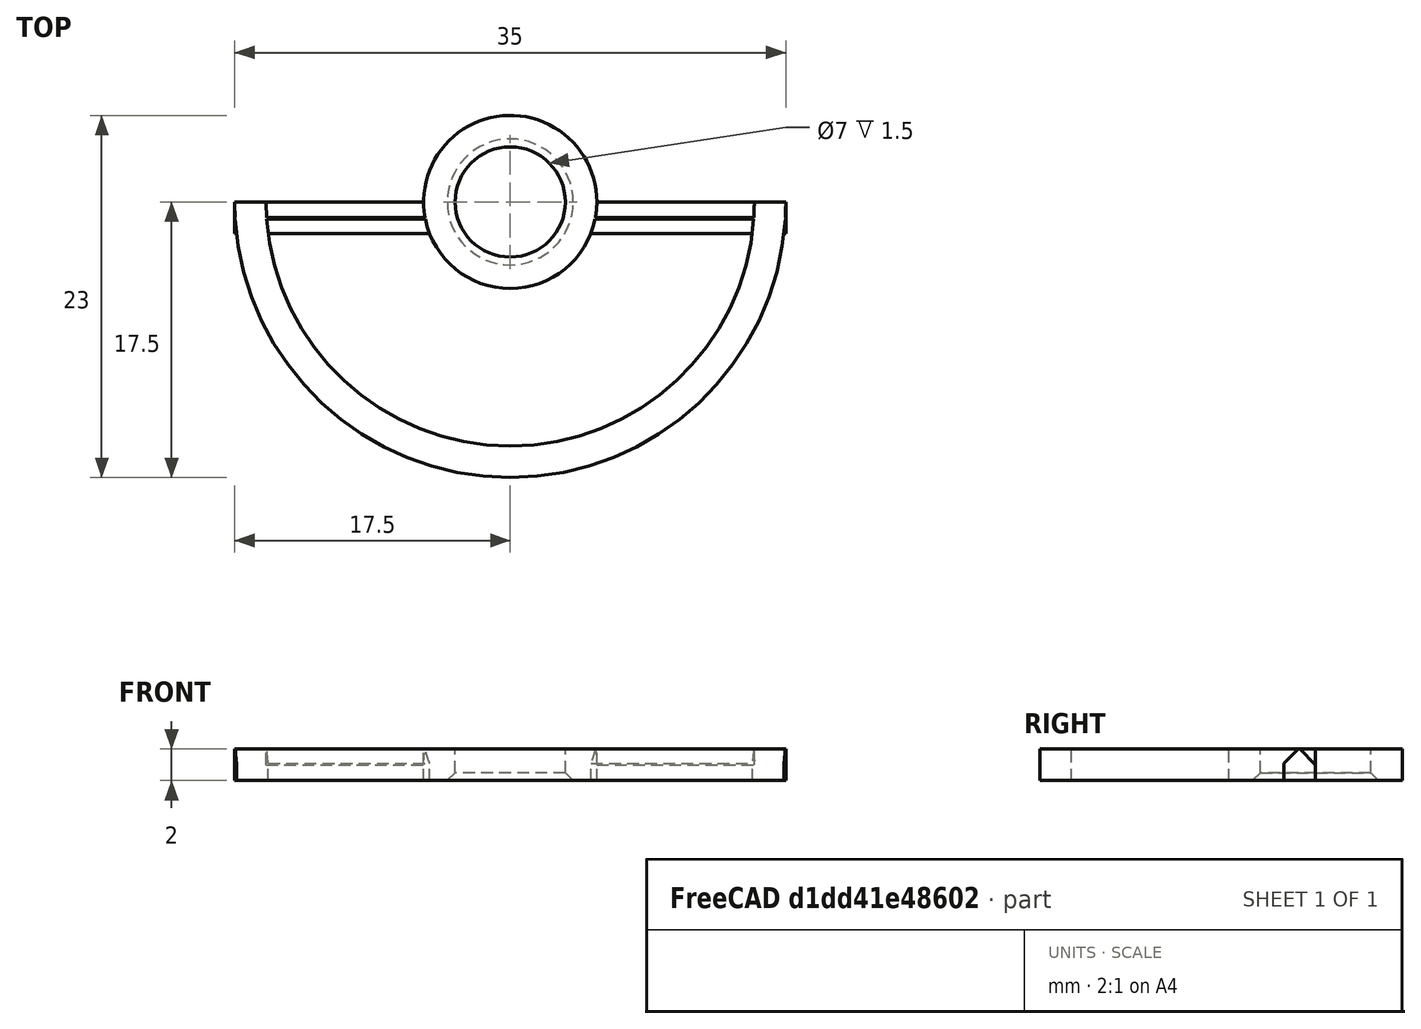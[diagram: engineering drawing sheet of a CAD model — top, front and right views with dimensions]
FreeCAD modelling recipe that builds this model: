
FCSTD DOCUMENT  (FreeCAD 0.16R6703 (Git))
Label: prop-guard
License: All rights reserved
LicenseURL: http://en.wikipedia.org/wiki/All_rights_reserved
objects: Part::Cylinder×5, Part::Chamfer×5, Part::Cut×4, Part::Box×2, Part::MultiFuse×1
note: 17 computed .brp shape members not serialized (recipe doc carries the construction recipe); baked Part::Feature solids carry a one-line shape summary decoded from their .brp

FEATURE [Part::Cylinder] Cylinder
  Angle = 360
  Height = 10
  Placement = pos=(0,0,-3) rot=(0,0,1;0rad)
  Radius = 3.5
FEATURE [Part::Cylinder] Cylinder001
  Angle = 360
  Height = 9
  Placement = pos=(0,0,-1) rot=(0,0,1;0rad)
  Radius = 15.5
FEATURE [Part::Cylinder] Cylinder002
  Angle = 360
  Height = 2
  Radius = 17.5
FEATURE [Part::Cut] Cut
  Base = -> Cylinder002
  Tool = -> Cylinder001
FEATURE [Part::Box] Box  label="Cube"
  Height = 10
  Length = 43
  Placement = pos=(-22,0,-1) rot=(0,0,1;0rad)
  Width = 27
FEATURE [Part::Cut] Cut001
  Base = -> Cut
  Tool = -> Box
FEATURE [Part::Box] Box001  label="Cube001"
  Height = 2
  Length = 35
  Placement = pos=(-17.5,-2,0) rot=(0,0,1;0rad)
  Width = 2
FEATURE [Part::Cylinder] Cylinder003
  Angle = 360
  Height = 2
  Radius = 5.5
FEATURE [Part::Cut] Cut002
  Base = -> Cylinder003
  Tool = -> Cylinder
FEATURE [Part::Cylinder] Cylinder004
  Angle = 360
  Height = 10
  Placement = pos=(0,0,-3) rot=(0,0,1;0rad)
  Radius = 5
FEATURE [Part::Cut] Cut003
  Base = -> Box001
  Tool = -> Cylinder004
FEATURE [Part::Chamfer] Chamfer
  Base = -> Cut003
  Edges = 1 edges r=1: [Edge22]
FEATURE [Part::Chamfer] Chamfer001
  Base = -> Chamfer
  Edges = 1 edges r=0.9: [Edge7]
FEATURE [Part::Chamfer] Chamfer002
  Base = -> Chamfer001
  Edges = 1 edges r=1: [Edge26]
FEATURE [Part::Chamfer] Chamfer003
  Base = -> Chamfer002
  Edges = 1 edges r=0.9: [Edge8]
FEATURE [Part::MultiFuse] Fusion  label="prop-guard-a"
  Shapes = -> [Chamfer003,Cut001,Cut002]
FEATURE [Part::Chamfer] Chamfer004  label="prop-guard"
  Base = -> Fusion
  Edges = 1 edges r=0.5: [Edge94]
